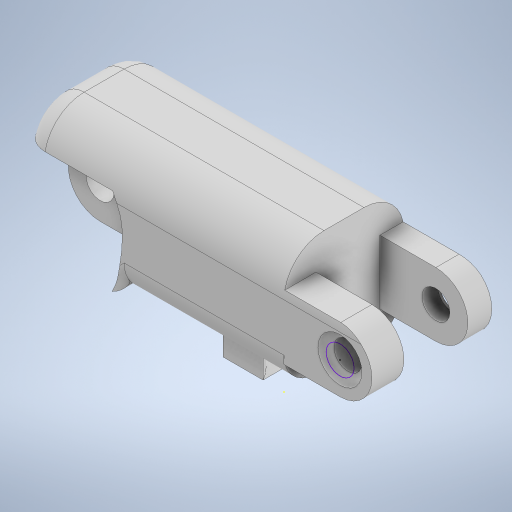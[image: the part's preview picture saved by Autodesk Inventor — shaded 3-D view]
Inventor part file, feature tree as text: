
AUTODESK INVENTOR PART (.ipt)
format: ipt  version: 2024 (Build 280153000, 153)  size: 560,640 bytes
history: native  units: mm
features: sketch x18, extrude x15, fillet x7, other x1
ambient origin geometry x8: Origin, YZ Plane, XZ Plane, XY Plane, X Axis, Y Axis, Z Axis, Center Point
bodies: Body1 (feature_tree)
feature tree (41):
  other  "Твердое тело1"
  extrude  "Выдавливание1"  Depth=15.0mm
  fillet  "Сопряжение1"  Radius=20.0mm
  extrude  "Выдавливание4"  Depth=15.0mm TaperAngle=0.0deg
  extrude  "Выдавливание5"  Depth=4.0mm
  extrude  "Выдавливание6"  Depth=8.0mm
  extrude  "Выдавливание7"  Depth=8.0mm
  extrude  "Выдавливание8"  Depth=4.0mm
  extrude  "Выдавливание9"  Depth=7.0mm
  extrude  "Выдавливание10"  Depth=3.5mm
  fillet  "Сопряжение4"  [1 undecoded]
  extrude  "Выдавливание11"  Depth=4.0mm
  extrude  "Выдавливание12"  Depth=4.0mm
  fillet  "Сопряжение6"  [1 undecoded]
  sketch  "Эскиз14"
  fillet  "Сопряжение7"  Radius=8.0mm
  fillet  "Сопряжение8"  Radius=8.0mm
  extrude  "Выдавливание13"  Depth=11.0mm
  extrude  "Выдавливание14"  Depth=4.0mm
  extrude  "Выдавливание15"  Depth=3.5mm
  sketch  "Эскиз18"
  sketch  "Эскиз19"
  extrude  "Выдавливание16"  TaperAngle=0.0deg  [1 undecoded]
  fillet  "Сопряжение9"  Radius=4.0mm
  fillet  "Сопряжение10"  Radius=4.0mm
  extrude  "Выдавливание17"  TaperAngle=0.0deg  [1 undecoded]
  sketch  "Эскиз1"
  sketch  "Эскиз4"
  sketch  "Эскиз5"
  sketch  "Эскиз7"
  sketch  "Эскиз8"
  sketch  "Эскиз9"
  sketch  "Эскиз10"
  sketch  "Эскиз11"
  sketch  "Эскиз12"
  sketch  "Эскиз13"
  sketch  "Эскиз15"
  sketch  "Эскиз16"
  sketch  "Эскиз17"
  sketch  "Эскиз20"
  sketch  "Эскиз21"
note: 4 required parameter values undecoded (feature->parameter linkage not recoverable at this tier; creation-order binding heuristic only, values carry confidence <= 0.55)
